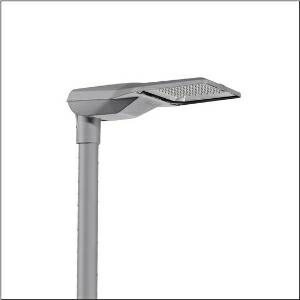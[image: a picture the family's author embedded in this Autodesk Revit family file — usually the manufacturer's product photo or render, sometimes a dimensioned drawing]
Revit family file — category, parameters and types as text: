
# Revit family: streetlight_sl_21_iq_midi___p0_8ab_5xe3r31g08nb_5ea3
name_source: partatom
category: Lighting Fixtures
units: mm (PartAtom-declared; Revit-internal decimal feet)

## family parameters
Cut with Voids When Loaded = No
Host = Face
Light Source = No
Part Type = Normal
Room Calculation Point = No
Round Connector Dimension = Use Diameter
Shared = No

## types (1)
- --- (1 x LED, 20170 lm, 155.5 W, 3000K)
    Apparent Load = 155 VA
    CIE Flux Codes = 39 72 97 100 100
    Color Rendering = 70
    Color Temperature = 3000K
    Default Elevation = 1800 mm
    Description = Streetlight SL 21 iQ midi, mast luminaire, primary light control with lens, of PMMA, primary optical cover: cover, of toughened safety glass, transparent, light distribution: P0.8aB, light emission: direct distribution, primary light characteristic: asymmetric, installation type: post-top, side-entry, LED, High Power LED, rated luminous flux: 20.170lm, luminous efficacy: 130lm/W, light colour: 730, colour temperature: 3000K, control gear: iQ Street-Remote, control: pre-setting: linear dimming characteristic, Street-Remote, Auto-Match, Temp-Guard, Lumen-Switch, Night-Set, Smart-Wire, Light-Fading, Desk-Remote (wireless, voltage-free reading and setting of iQ features in the workshop via application-optimized NFC function/RFID function), optimised constant luminous flux control (CLO 2.0), mains connection: 230..240V, AC, 50/60Hz, start of lifetime: 156W, end of service life: 162W, reduction: 69W, luminaire housing, of diecast aluminium, powder-coated, SITECO metallic grey (DB 702S), corrosivity category C5 high according to DIN EN ISO 12944, please order mast flange separately, inclination adjustable: 0°, 5°, 10°, 15°, sealing non-destructively replaceable, multi-level sealing system, length: 644mm, width: 335mm, height: 110mm, mast flange for spigot size: 42mm (side-entry): 5XC10008XM4, 60/48mm (side-entry/post-top): 5XC10108XM2, 76/60mm (side-entry/post-top): 5XC10108XM1, mounting height: 4..8m, protection rating (complete): IP66, insulation class (complete): insulation class II (safety insulation), certification: CE, ENEC, ENEC+, VDE, impact resistance: IK10, permissible operating ambient temperature for outdoor applications: -40..+50°C, standard-compliant lighting for roads and squares, packaging unit: 1 piece

Light Distribution: P0.8aB
    Height = 111 mm
    Lamp = 1 x LED
    Lamp Light Flux = 20170 lm
    Lamp Power = 155.5 W
    Lamp count = 1
    Length = 644 mm
    Luminous efficacy = 130 lm/W
    Manufacturer = Siteco
    ModVariant = No
    Model = 5XE3R31G08NB
    Number of Poles = 1
    OnlyDefault = Yes
    Power Factor = 1
    Product Name = Streetlight SL 21 iQ midi | P0.8aB
    Product group = mast luminaire | pylon top
    ProductGroupID = 6100
    Protection Class = Protection class II
    Protection Degree = IP 66
    RLX_Detail_Level = 1
    RLX_Emergency_Light_Flux = 0 lm
    RLX_Emergency_Type = 0
    RLX_Emergency_Type_DB = No
    RlxData = <blob elided: 90157 chars, md5=3b36a5fa>
    Socket = socket
    Standby Power = 0 W
    System Light Flux = 20170 lm
    System Power = 155 W
    Type Comments = factory setting: luminous flux: 100 % | dim-lin: 254 | 823 mA
    Type Image = l_1004298.jpg
    URL = http://relux.com
    VarID = @adj_078759
    Voltage = 0 V
    Weight = 0.00 kg
    Width = 336 mm

## geometry (parser evidence)
native form markers: Blend x4, Sweep x11
no freeform markers — native parametric forms only
